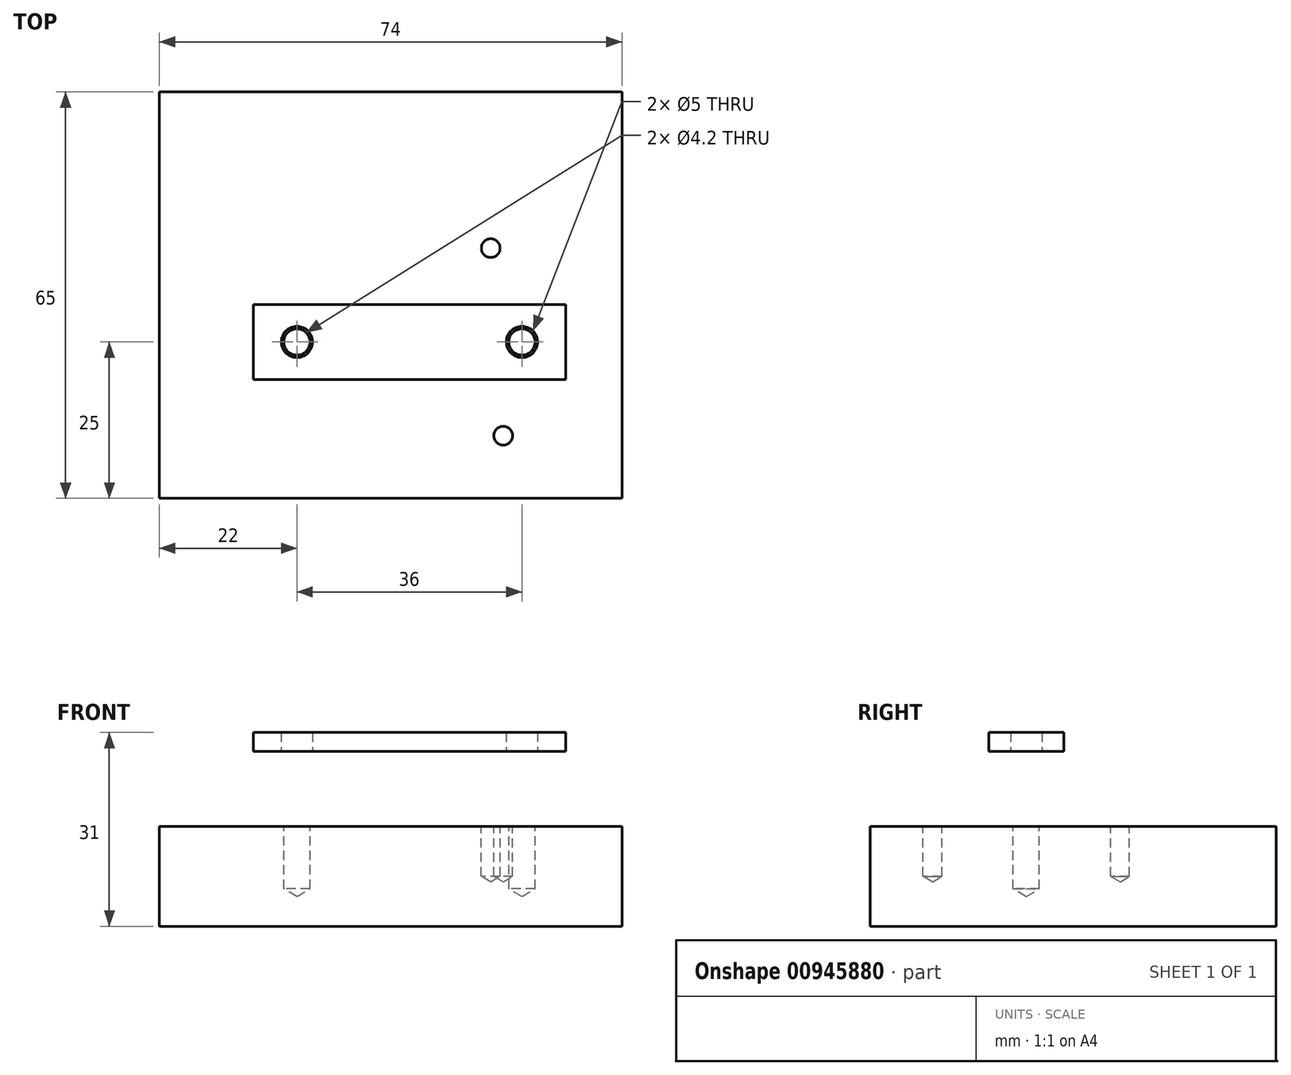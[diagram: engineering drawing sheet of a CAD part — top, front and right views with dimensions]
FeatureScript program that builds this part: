
annotation { "Feature Type Name" : "Feature", "Feature Type Description" : "" }
export const myFeature = defineFeature(function(context is Context, id is Id, definition is map)
    precondition{}
    {
        {
            var Q0;
            Q0=qCreatedBy(makeId("Top.planeOp"),FACE);
            var sketch = newSketch(context, id + "F0", { "sketchPlane" : qUnion([Q0])});
            skLineSegment(sketch, "E0.bottom", {"start": v(37, 32.5) * mm, "end": v(-37, 32.5) * mm});
            skLineSegment(sketch, "E0.top", {"start": v(37, -32.5) * mm, "end": v(-37, -32.5) * mm});
            skLineSegment(sketch, "E0.left", {"start": v(37, 32.5) * mm, "end": v(37, -32.5) * mm});
            skLineSegment(sketch, "E0.right", {"start": v(-37, 32.5) * mm, "end": v(-37, -32.5) * mm});
            skPoint(sketch, "E0.middle", {"position": v(0, 0) * mm});
            skSolve(sketch);
        }
        {
            var Q0;
            Q0 = qSketchRegion(id + "F0", true);
            extrude(context, id + "F1", {"entities" : qUnion([Q0]), "oppositeDirection" : true, "depth" : 16 * mm, "offsetDistance" : 25 * mm});
        }
        {
            var Q0;
            Q0=makeQuery(id+"F1.opExtrude","CAP_FACE",FACE,{"disambiguationData":[OSD([sQuery(id+"F0.wireOp",EDGE,"E0.bottom"),sQuery(id+"F0.wireOp",EDGE,"E0.top"),sQuery(id+"F0.wireOp",EDGE,"E0.left"),sQuery(id+"F0.wireOp",EDGE,"E0.right")])],"isStart":true});
            var sketch = newSketch(context, id + "F2", { "sketchPlane" : qUnion([Q0])});
            skPoint(sketch, "E1", {"position": v(16, 7.5) * mm});
            skPoint(sketch, "E2", {"position": v(18, -22.5) * mm});
            skPoint(sketch, "E3", {"position": v(21, -7.5) * mm});
            skPoint(sketch, "E4", {"position": v(-15, -7.5) * mm});
            skSolve(sketch);
        }
        {
            var Q0;
            Q0=sQuery(id+"F2.wireOp",VERTEX,"E2");
            var Q1;
            Q1=sQuery(id+"F2.wireOp",VERTEX,"E1");
            var Q2;
            Q2=makeQuery(id+"F1.opExtrude","SWEPT_BODY",BODY,{"disambiguationData":[OSD([sQuery(id+"F0.wireOp",EDGE,"E0.bottom"),sQuery(id+"F0.wireOp",EDGE,"E0.top"),sQuery(id+"F0.wireOp",EDGE,"E0.left"),sQuery(id+"F0.wireOp",EDGE,"E0.right")])]});
            hole(context, id + "F3", {"style" : HoleStyle.SIMPLE, "endStyle" : HoleEndStyle.BLIND, "standardTappedOrClearance" : lookupTablePath({ "standard" : "ISO", "size" : "3", "type" : "Drilled" }), "standardBlindInLast" : lookupTablePath({ "standard" : "ISO", "size" : "3", "type" : "Drilled" }), "holeDiameter" : 3 * mm, "majorDiameter" : 5 * mm, "holeDepth" : 8 * mm, "tappedDepth" : 11.9 * mm, "tapClearance" : 3, "locations" : qUnion([Q0, Q1]), "scope" : qUnion([Q2])});
        }
        {
            var Q0;
            Q0=sQuery(id+"F2.wireOp",VERTEX,"E3");
            var Q1;
            Q1=sQuery(id+"F2.wireOp",VERTEX,"E4");
            var Q2;
            Q2=makeQuery(id+"F1.opExtrude","SWEPT_BODY",BODY,{"disambiguationData":[OSD([sQuery(id+"F0.wireOp",EDGE,"E0.bottom"),sQuery(id+"F0.wireOp",EDGE,"E0.top"),sQuery(id+"F0.wireOp",EDGE,"E0.left"),sQuery(id+"F0.wireOp",EDGE,"E0.right")])]});
            hole(context, id + "F4", {"style" : HoleStyle.SIMPLE, "endStyle" : HoleEndStyle.BLIND, "standardTappedOrClearance" : lookupTablePath({ "standard" : "ISO", "engagement" : "75%", "pitch" : "0.8 mm", "size" : "M5", "type" : "Tapped" }), "standardBlindInLast" : lookupTablePath({ "standard" : "ISO", "fit" : "Normal", "engagement" : "75%", "pitch" : "0.8 mm", "size" : "M5", "type" : "Clearance & tapped" }), "holeDiameter" : 4.2 * mm, "majorDiameter" : 5 * mm, "showTappedDepth" : true, "holeDepth" : 10 * mm, "tappedDepth" : 7.6 * mm, "tapClearance" : 3, "locations" : qUnion([Q0, Q1]), "scope" : qUnion([Q2])});
        }
        {
            var Q0;
            Q0=makeQuery(id+"F2.imprint","IMPRINT",FACE,{"disambiguationData":[TD([[makeQuery(id+"F2.imprint","IMPRINT",EDGE,{"derivedFrom":makeQuery(id+"F1.opExtrude","CAP_EDGE",EDGE,{"disambiguationData":[OSD([sQuery(id+"F0.wireOp",EDGE,"E0.bottom")])],"isStart":true})}),1.0]])]});
            cPlane(context, id + "F5", {"entities" : qUnion([Q0]), "cplaneType" : CPlaneType.OFFSET, "offset" : 12 * mm, "width" : 150 * mm, "height" : 150 * mm});
        }
        {
            var Q0;
            Q0=qCreatedBy(id+"F5.planeOp",FACE);
            var sketch = newSketch(context, id + "F6", { "sketchPlane" : qUnion([Q0])});
            skPoint(sketch, "E5", {"position": v(-15, -7.5) * mm});
            skPoint(sketch, "E6", {"position": v(21, -7.5) * mm});
            skSolve(sketch);
        }
        {
            var Q0;
            Q0=qCreatedBy(id+"F5.planeOp",FACE);
            var sketch = newSketch(context, id + "F7", { "sketchPlane" : qUnion([Q0])});
            skLineSegment(sketch, "E7.bottom", {"start": v(-22, -1.5) * mm, "end": v(28, -1.5) * mm});
            skLineSegment(sketch, "E7.top", {"start": v(-22, -13.5) * mm, "end": v(28, -13.5) * mm});
            skLineSegment(sketch, "E7.left", {"start": v(-22, -1.5) * mm, "end": v(-22, -13.5) * mm});
            skLineSegment(sketch, "E7.right", {"start": v(28, -1.5) * mm, "end": v(28, -13.5) * mm});
            skLineSegment(sketch, "E8", {"start": v(3, -1.5) * mm, "end": v(3, -13.5) * mm, "construction": true});
            skLineSegment(sketch, "E9", {"start": v(-22, -7.5) * mm, "end": v(28, -7.5) * mm, "construction": true});
            skSolve(sketch);
        }
        {
            var Q0;
            Q0 = qSketchRegion(id + "F7", true);
            extrude(context, id + "F8", {"entities" : qUnion([Q0]), "depth" : 3 * mm, "offsetDistance" : 25 * mm});
        }
        {
            var Q0;
            Q0=sQuery(id+"F6.wireOp",VERTEX,"E5");
            var Q1;
            Q1=sQuery(id+"F6.wireOp",VERTEX,"E6");
            var Q2;
            Q2=makeQuery(id+"F8.opExtrude","SWEPT_BODY",BODY,{"disambiguationData":[OSD([sQuery(id+"F7.wireOp",EDGE,"E7.bottom"),sQuery(id+"F7.wireOp",EDGE,"E7.top"),sQuery(id+"F7.wireOp",EDGE,"E7.left"),sQuery(id+"F7.wireOp",EDGE,"E7.right")])]});
            hole(context, id + "F9", {"style" : HoleStyle.SIMPLE, "endStyle" : HoleEndStyle.BLIND, "oppositeDirection" : true, "standardTappedOrClearance" : lookupTablePath({ "standard" : "ISO", "size" : "5", "type" : "Drilled" }), "standardBlindInLast" : lookupTablePath({ "standard" : "ISO", "size" : "5", "type" : "Drilled" }), "holeDiameter" : 5 * mm, "majorDiameter" : 5 * mm, "holeDepth" : 8 * mm, "tappedDepth" : 11.9 * mm, "tapClearance" : 3, "locations" : qUnion([Q0, Q1]), "scope" : qUnion([Q2])});
        }
    });
